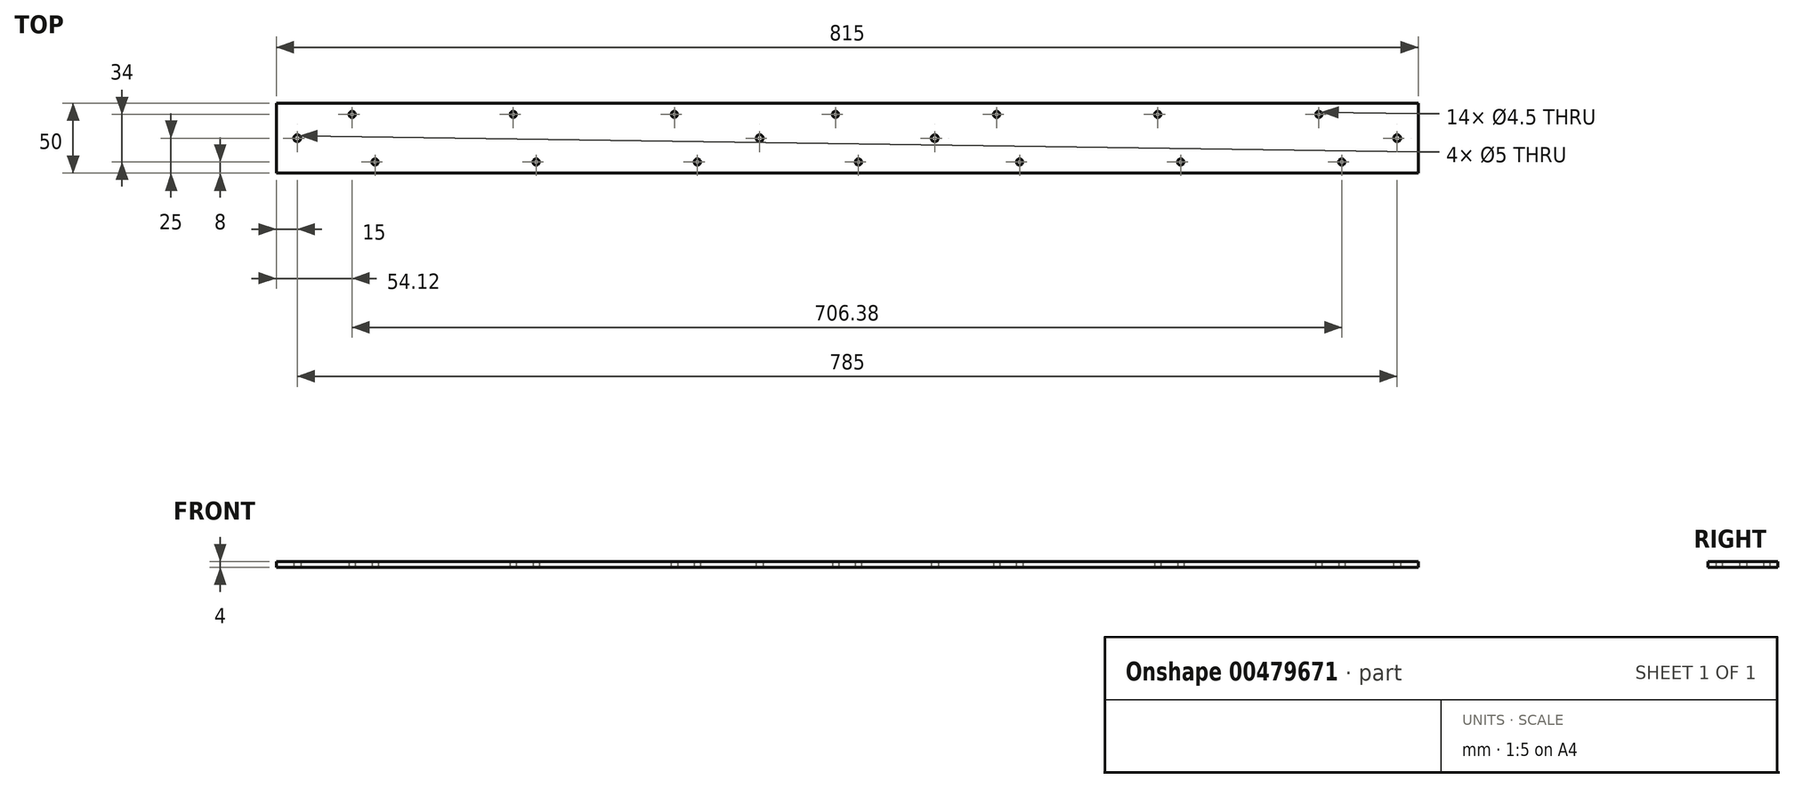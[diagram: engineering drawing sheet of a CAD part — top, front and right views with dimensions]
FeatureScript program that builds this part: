
annotation { "Feature Type Name" : "Feature", "Feature Type Description" : "" }
export const myFeature = defineFeature(function(context is Context, id is Id, definition is map)
    precondition{}
    {
        {
            var Q0;
            Q0=qCreatedBy(makeId("Top.planeOp"),FACE);
            var sketch = newSketch(context, id + "F0", { "sketchPlane" : qUnion([Q0])});
            skLineSegment(sketch, "E0.bottom", {"start": v(-407.5, 25) * mm, "end": v(407.5, 25) * mm});
            skLineSegment(sketch, "E0.top", {"start": v(-407.5, -25) * mm, "end": v(407.5, -25) * mm});
            skLineSegment(sketch, "E0.left", {"start": v(-407.5, 25) * mm, "end": v(-407.5, -25) * mm});
            skLineSegment(sketch, "E0.right", {"start": v(407.5, 25) * mm, "end": v(407.5, -25) * mm});
            skPoint(sketch, "E0.middle", {"position": v(0, 0) * mm});
            skCircle(sketch, "E1", {"center": v(-353.38, 17) * mm, "radius": 2.25 * mm});
            skCircle(sketch, "E2", {"center": v(-337, -17) * mm, "radius": 2.25 * mm});
            skCircle(sketch, "E3.1.0.0", {"center": v(-238.38, 17) * mm, "radius": 2.25 * mm});
            skCircle(sketch, "E3.1.0.1", {"center": v(-222, -17) * mm, "radius": 2.25 * mm});
            skCircle(sketch, "E3.2.0.0", {"center": v(-123.38, 17) * mm, "radius": 2.25 * mm});
            skCircle(sketch, "E3.2.0.1", {"center": v(-107, -17) * mm, "radius": 2.25 * mm});
            skCircle(sketch, "E3.3.0.0", {"center": v(-8.38, 17) * mm, "radius": 2.25 * mm});
            skCircle(sketch, "E3.3.0.1", {"center": v(8, -17) * mm, "radius": 2.25 * mm});
            skCircle(sketch, "E3.4.0.0", {"center": v(106.62, 17) * mm, "radius": 2.25 * mm});
            skCircle(sketch, "E3.4.0.1", {"center": v(123, -17) * mm, "radius": 2.25 * mm});
            skCircle(sketch, "E3.5.0.0", {"center": v(221.62, 17) * mm, "radius": 2.25 * mm});
            skCircle(sketch, "E3.5.0.1", {"center": v(238, -17) * mm, "radius": 2.25 * mm});
            skCircle(sketch, "E3.6.0.0", {"center": v(336.62, 17) * mm, "radius": 2.25 * mm});
            skCircle(sketch, "E3.6.0.1", {"center": v(353, -17) * mm, "radius": 2.25 * mm});
            skLineSegment(sketch, "E3.direction1", {"start": v(-353.38, 17) * mm, "end": v(-238.38, 17) * mm, "construction": true});
            skPoint(sketch, "E4", {"position": v(-392.5, 0) * mm});
            skPoint(sketch, "E4.positionSnap0", {"position": v(-407.5, 0) * mm});
            skPoint(sketch, "E5", {"position": v(392.5, 0) * mm});
            skPoint(sketch, "E5.positionSnap0", {"position": v(407.5, 0) * mm});
            skPoint(sketch, "E6", {"position": v(62.5, 0) * mm});
            skPoint(sketch, "E7", {"position": v(-62.5, 0) * mm});
            skSolve(sketch);
        }
        {
            var Q0;
            Q0 = qSketchRegion(id + "F0", true);
            extrude(context, id + "F1", {"entities" : qUnion([Q0]), "depth" : 4 * mm, "offsetDistance" : 25 * mm});
        }
        {
            var Q0;
            Q0=sQuery(id+"F0.wireOp",VERTEX,"E4");
            var Q1;
            Q1=sQuery(id+"F0.wireOp",VERTEX,"E7");
            var Q2;
            Q2=sQuery(id+"F0.wireOp",VERTEX,"E6");
            var Q3;
            Q3=sQuery(id+"F0.wireOp",VERTEX,"E5");
            var Q4;
            Q4=makeQuery(id+"F1.opExtrude","SWEPT_BODY",BODY,{"disambiguationData":[OSD([sQuery(id+"F0.wireOp",EDGE,"E0.bottom"),sQuery(id+"F0.wireOp",EDGE,"E0.top"),sQuery(id+"F0.wireOp",EDGE,"E0.left"),sQuery(id+"F0.wireOp",EDGE,"E0.right"),sQuery(id+"F0.wireOp",EDGE,"E1"),sQuery(id+"F0.wireOp",EDGE,"E2"),sQuery(id+"F0.wireOp",EDGE,"E3.1.0.0"),sQuery(id+"F0.wireOp",EDGE,"E3.1.0.1"),sQuery(id+"F0.wireOp",EDGE,"E3.2.0.0"),sQuery(id+"F0.wireOp",EDGE,"E3.2.0.1"),sQuery(id+"F0.wireOp",EDGE,"E3.3.0.0"),sQuery(id+"F0.wireOp",EDGE,"E3.3.0.1"),sQuery(id+"F0.wireOp",EDGE,"E3.4.0.0"),sQuery(id+"F0.wireOp",EDGE,"E3.4.0.1"),sQuery(id+"F0.wireOp",EDGE,"E3.5.0.0"),sQuery(id+"F0.wireOp",EDGE,"E3.5.0.1"),sQuery(id+"F0.wireOp",EDGE,"E3.6.0.0"),sQuery(id+"F0.wireOp",EDGE,"E3.6.0.1")])]});
            hole(context, id + "F2", {"style" : HoleStyle.SIMPLE, "endStyle" : HoleEndStyle.THROUGH, "oppositeDirection" : true, "holeDiameter" : 5 * mm, "majorDiameter" : 5 * mm, "isTappedThrough" : true, "tappedDepth" : 12 * mm, "tapClearance" : 3, "locations" : qUnion([Q0, Q1, Q2, Q3]), "scope" : qUnion([Q4])});
        }
    });
